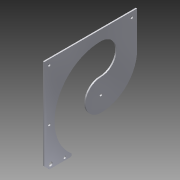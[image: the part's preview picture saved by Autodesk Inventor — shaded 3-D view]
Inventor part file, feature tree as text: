
AUTODESK INVENTOR PART (.ipt)
format: ipt  version: 2015 (Build 190159000, 159)  size: 204,288 bytes
history: native  units: in
note: dims shown in document units (in); Inventor stores cm internally (conversion verified against a paired STEP export)
features: sketch x6, projected_geometry x5, extrude x4, hole x2, fillet x1
ambient origin geometry x8: Origin, YZ Plane, XZ Plane, XY Plane, X Axis, Y Axis, Z Axis, Center Point
bodies: Solid1 (feature_tree)
feature tree (18):
  extrude  "Extrusion1"  Depth=2.5in
  extrude  "Extrusion2"  Depth=3.25in
  hole  "Hole1"  [1 undecoded]
  sketch  "Sketch4"  dims[d6=0.0in d7=9.0in]
  extrude  "Extrusion4"  Depth=9.0in
  hole  "Hole3"  [1 undecoded]
  fillet  "Fillet1"  Radius=7.0in
  extrude  "Extrusion5"  Depth=0.125in
  sketch  "Sketch1"  dims[d0=4.0in d1=2.5in]
  sketch  "Sketch2"  dims[d2=2.5in d3=3.25in]
  projected_geometry  "Projected Loop1"
  sketch  "Sketch3"  dims[d4=3.25in d5=0.0in]
  projected_geometry  "Projected Loop2"
  projected_geometry  "Projected Loop3"
  sketch  "Sketch5"  dims[d8=3.0in d9=3.0in d10=7.0in]
  projected_geometry  "Projected Loop4"
  sketch  "Sketch6"  dims[d11=3.5in d12=5.5in d13=0.0in d14=9.5in d15=5.5in d16=0.0in d22=0.125in d23=0.0in d24=3.0in d25=0.25in d26=0.5in d27=0.125in d28=0.0in d29=0.5in d30=0.5in d31=0.5in d32=0.5in d33=0.5in d34=5.5in d35=3.75in d36=3.25in d37=0.25in d38=0.75in d39=0.375in d40=0.25in d41=0.5635in d42=1.0in d43=0.8108in d55=0.25in d60=0.5in d61=0.5in d62=0.125in d63=0.0in d64=0.625in d65=0.375in d66=0.375in d67=0.75in d68=0.375in d69=0.25in d70=0.5635in d71=1.0in d72=0.8108in d73=0.125in d74=1.0in d75=0.0in d76=0.25in d77=1.7in]
  projected_geometry  "Projected Loop5"
note: 2 required parameter values undecoded (feature->parameter linkage not recoverable at this tier; creation-order binding heuristic only, values carry confidence <= 0.55)
